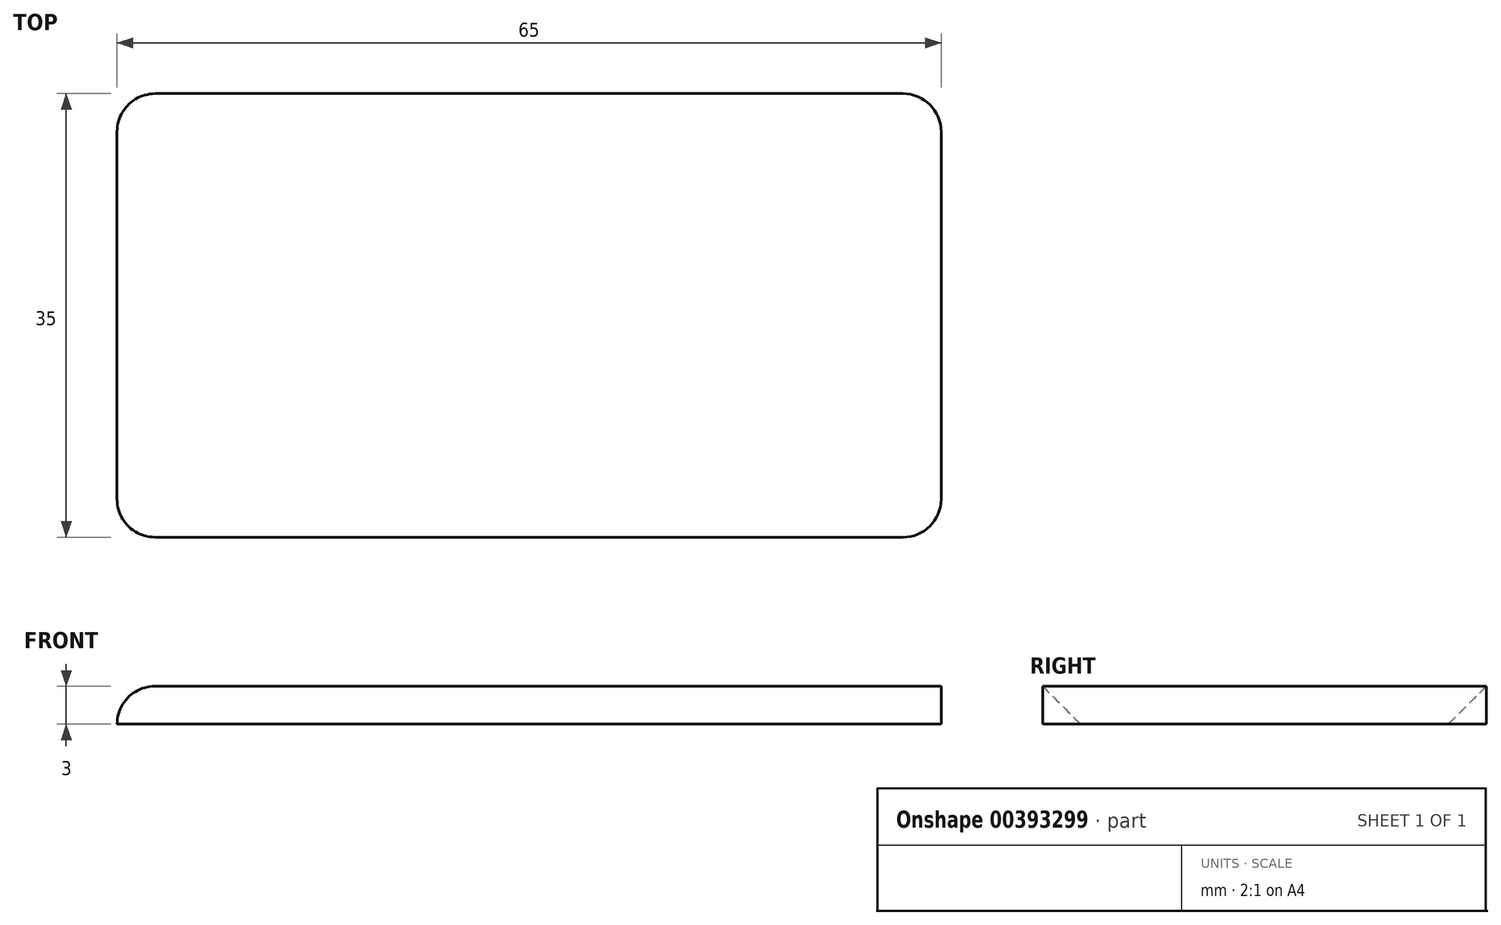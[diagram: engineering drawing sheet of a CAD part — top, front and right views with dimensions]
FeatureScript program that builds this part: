
annotation { "Feature Type Name" : "Feature", "Feature Type Description" : "" }
export const myFeature = defineFeature(function(context is Context, id is Id, definition is map)
    precondition{}
    {
        {
            var Q0;
            Q0=qCreatedBy(makeId("Top.planeOp"),FACE);
            var sketch = newSketch(context, id + "F0", { "sketchPlane" : qUnion([Q0])});
            skLineSegment(sketch, "E0.bottom", {"start": v(32.5, 17.5) * mm, "end": v(-32.5, 17.5) * mm});
            skLineSegment(sketch, "E0.top", {"start": v(32.5, -17.5) * mm, "end": v(-32.5, -17.5) * mm});
            skLineSegment(sketch, "E0.left", {"start": v(32.5, 17.5) * mm, "end": v(32.5, -17.5) * mm});
            skLineSegment(sketch, "E0.right", {"start": v(-32.5, 17.5) * mm, "end": v(-32.5, -17.5) * mm});
            skPoint(sketch, "E0.middle", {"position": v(0, 0) * mm});
            skSolve(sketch);
        }
        {
            var Q0;
            Q0 = qSketchRegion(id + "F0", true);
            extrude(context, id + "F1", {"entities" : qUnion([Q0]), "oppositeDirection" : true, "depth" : 3 * mm, "offsetDistance" : 25 * mm});
        }
        {
            var Q0;
            Q0=makeQuery(id+"F1.opExtrude","SWEPT_EDGE",EDGE,{"disambiguationData":[OSD([sQuery(id+"F0.wireOp",EDGE,"E0.top"),sQuery(id+"F0.wireOp",EDGE,"E0.right")])]});
            var Q1;
            Q1=makeQuery(id+"F1.opExtrude","SWEPT_EDGE",EDGE,{"disambiguationData":[OSD([sQuery(id+"F0.wireOp",EDGE,"E0.bottom"),sQuery(id+"F0.wireOp",EDGE,"E0.right")])]});
            var Q2;
            Q2=makeQuery(id+"F1.opExtrude","SWEPT_EDGE",EDGE,{"disambiguationData":[OSD([sQuery(id+"F0.wireOp",EDGE,"E0.bottom"),sQuery(id+"F0.wireOp",EDGE,"E0.left")])]});
            var Q3;
            Q3=makeQuery(id+"F1.opExtrude","SWEPT_EDGE",EDGE,{"disambiguationData":[OSD([sQuery(id+"F0.wireOp",EDGE,"E0.top"),sQuery(id+"F0.wireOp",EDGE,"E0.left")])]});
            fillet(context, id + "F2", {"entities" : qUnion([Q0, Q1, Q2, Q3]), "radius" : 3 * mm, "tangentPropagation" : true, "allowEdgeOverflow" : false});
        }
        {
            var Q0;
            Q0=makeQuery(id+"F1.opExtrude","CAP_EDGE",EDGE,{"disambiguationData":[OSD([sQuery(id+"F0.wireOp",EDGE,"E0.right")])],"isStart":true});
            fillet(context, id + "F3", {"entities" : qUnion([Q0]), "radius" : 3 * mm, "allowEdgeOverflow" : false});
        }
    });
